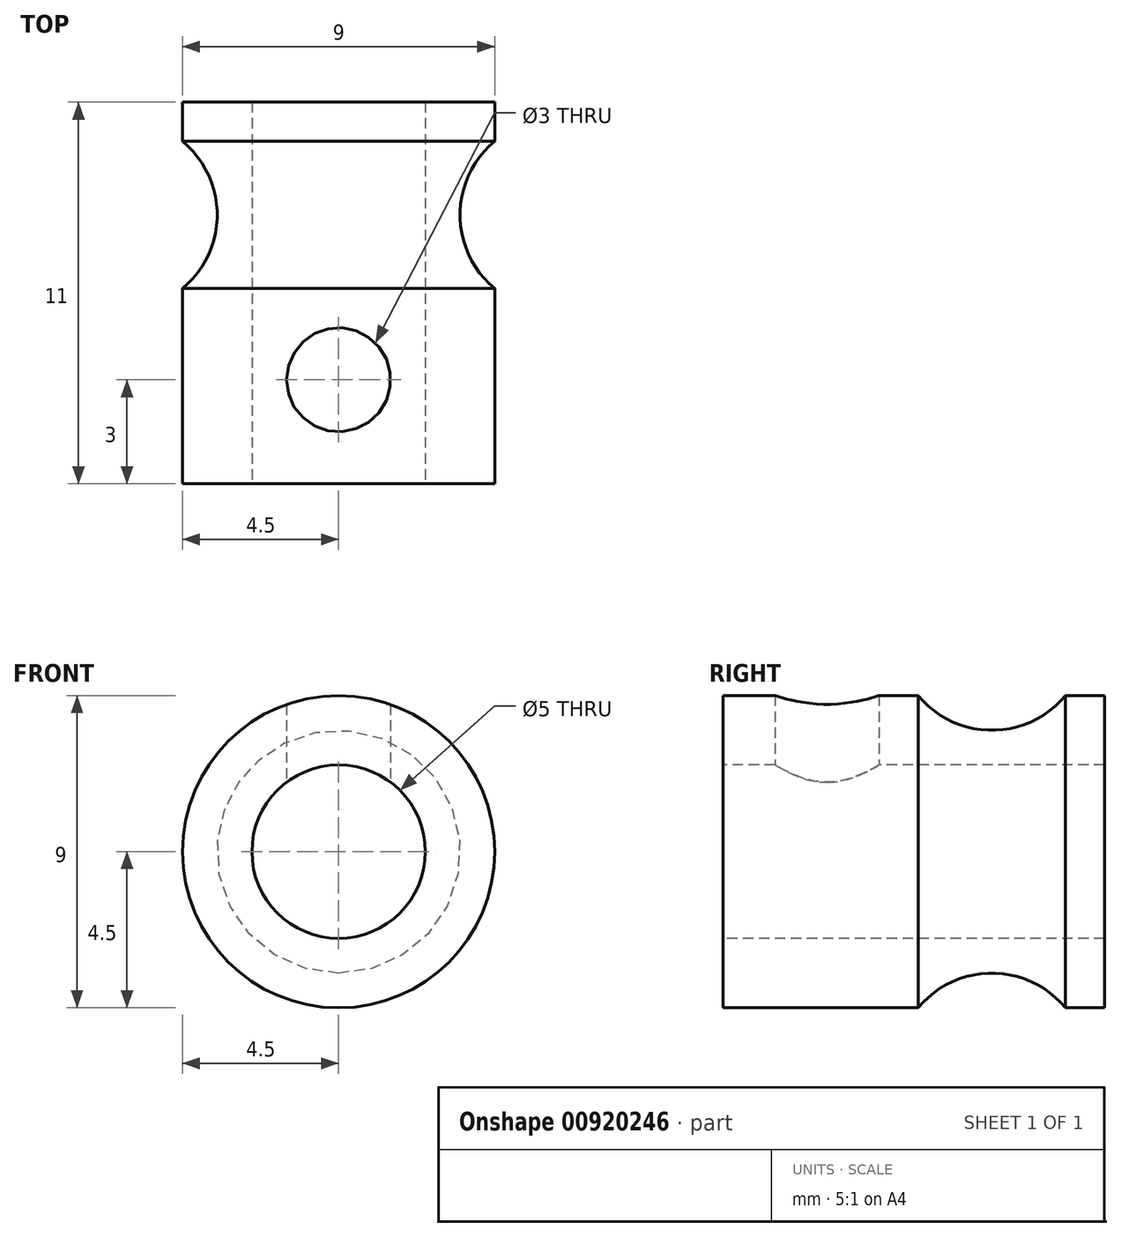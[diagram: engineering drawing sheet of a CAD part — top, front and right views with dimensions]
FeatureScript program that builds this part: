
annotation { "Feature Type Name" : "Feature", "Feature Type Description" : "" }
export const myFeature = defineFeature(function(context is Context, id is Id, definition is map)
    precondition{}
    {
        {
            var Q0;
            Q0=qCreatedBy(makeId("Top.planeOp"),FACE);
            var sketch = newSketch(context, id + "F0", { "sketchPlane" : qUnion([Q0])});
            skLineSegment(sketch, "E0", {"start": v(2.5, 0) * mm, "end": v(2.5, 11) * mm});
            skLineSegment(sketch, "E1", {"start": v(2.5, 11) * mm, "end": v(4.5, 11) * mm});
            skLineSegment(sketch, "E2", {"start": v(4.5, 11) * mm, "end": v(4.5, 9.87) * mm});
            skLineSegment(sketch, "E3", {"start": v(2.5, 0) * mm, "end": v(4.5, 0) * mm});
            skLineSegment(sketch, "E4", {"start": v(4.5, 0) * mm, "end": v(4.5, 5.62) * mm});
            skArc(sketch, "E5", {"start": v(4.5, 9.87) * mm, "mid": v(3.5, 7.75) * mm, "end": v(4.5, 5.62) * mm});
            skLineSegment(sketch, "E6", {"start": v(0, 0) * mm, "end": v(0, 11) * mm, "construction": true});
            skLineSegment(sketch, "E7.0", {"start": v(3.5, 0) * mm, "end": v(3.5, 11) * mm, "construction": true});
            skSolve(sketch);
        }
        {
            var Q0;
            Q0=qSketchRegion(id+"F0",true);
            var Q1;
            Q1=sQuery(id+"F0.wireOp",EDGE,"E6");
            revolve(context, id + "F1", {"surfaceOperationType" : NewSurfaceOperationType.NEW, "entities" : qUnion([Q0]), "axis" : qUnion([Q1]), "revolveType" : RevolveType.FULL});
        }
        {
            var Q0;
            Q0=qCreatedBy(makeId("Top.planeOp"),FACE);
            var sketch = newSketch(context, id + "F2", { "sketchPlane" : qUnion([Q0])});
            skCircle(sketch, "E8", {"center": v(0, 3) * mm, "radius": 1.5 * mm});
            skSolve(sketch);
        }
        {
            var Q0;
            Q0=makeQuery(id+"F2.imprint","IMPRINT",FACE,{"disambiguationData":[TD([[makeQuery(id+"F2.imprint","IMPRINT",EDGE,{"derivedFrom":sQuery(id+"F2.wireOp",EDGE,"E8")}),1.0]])]});
            extrude(context, id + "F3", {"entities" : qUnion([Q0]), "operationType" : NewBodyOperationType.REMOVE, "endBound" : BoundingType.THROUGH_ALL, "depth" : 25 * mm, "offsetDistance" : 25 * mm});
        }
    });
